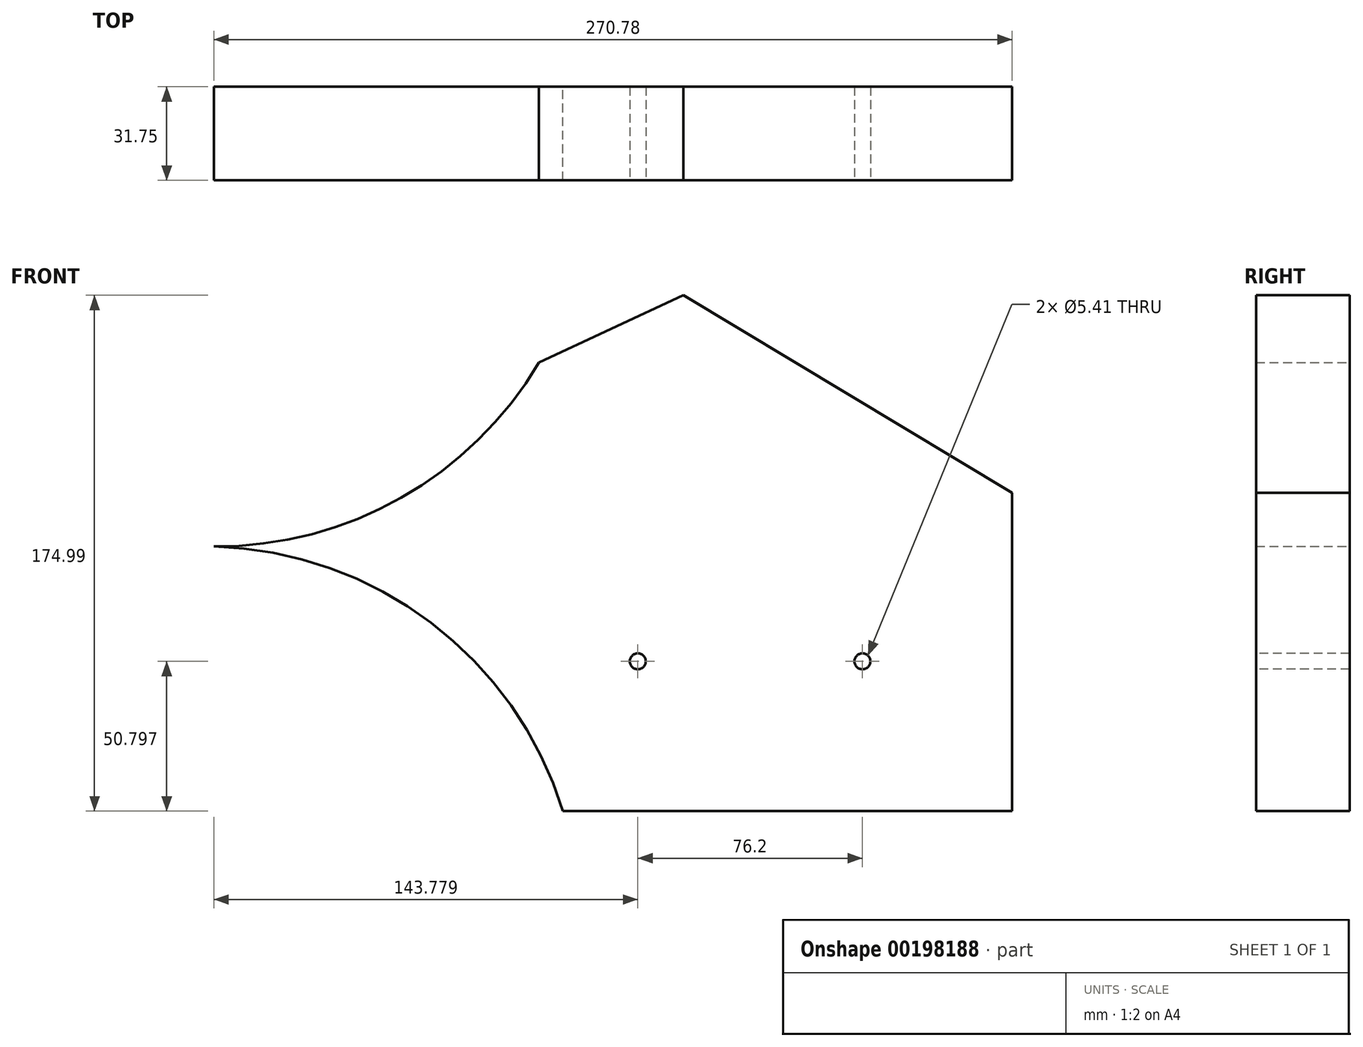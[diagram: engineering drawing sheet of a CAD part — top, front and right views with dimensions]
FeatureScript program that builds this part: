
annotation { "Feature Type Name" : "Feature", "Feature Type Description" : "" }
export const myFeature = defineFeature(function(context is Context, id is Id, definition is map)
    precondition{}
    {
        {
            var Q0;
            Q0=qCreatedBy(makeId("Front.planeOp"),FACE);
            var sketch = newSketch(context, id + "F0", { "sketchPlane" : qUnion([Q0])});
            skLineSegment(sketch, "E0", {"start": v(110.28, 62.43) * mm, "end": v(159.2, 85.24) * mm});
            skLineSegment(sketch, "E1", {"start": v(159.2, 85.24) * mm, "end": v(270.78, 18.2) * mm});
            skLineSegment(sketch, "E2", {"start": v(270.78, 18.2) * mm, "end": v(270.78, -89.75) * mm});
            skLineSegment(sketch, "E3", {"start": v(270.78, -89.75) * mm, "end": v(118.38, -89.75) * mm});
            skArc(sketch, "E4", {"start": v(0, 0) * mm, "mid": v(63.46, 16.52) * mm, "end": v(110.28, 62.43) * mm});
            skArc(sketch, "E5", {"start": v(118.38, -89.75) * mm, "mid": v(73.64, -25.82) * mm, "end": v(0, 0) * mm});
            skSolve(sketch);
        }
        {
            var Q0;
            Q0=makeQuery(id+"F0.imprint","IMPRINT",FACE,{"disambiguationData":[TD([[makeQuery(id+"F0.imprint","IMPRINT",EDGE,{"derivedFrom":sQuery(id+"F0.wireOp",EDGE,"E0")}),-1.0]])]});
            extrude(context, id + "F1", {"entities" : qUnion([Q0]), "depth" : 31.75 * mm});
        }
        {
            var Q0;
            Q0=makeQuery(id+"F1.opExtrude","CAP_FACE",FACE,{"disambiguationData":[OSD([sQuery(id+"F0.wireOp",EDGE,"E0"),sQuery(id+"F0.wireOp",EDGE,"E1"),sQuery(id+"F0.wireOp",EDGE,"E2"),sQuery(id+"F0.wireOp",EDGE,"E3"),sQuery(id+"F0.wireOp",EDGE,"E4"),sQuery(id+"F0.wireOp",EDGE,"E5")])],"isStart":false});
            var sketch = newSketch(context, id + "F2", { "sketchPlane" : qUnion([Q0])});
            skPoint(sketch, "E6", {"position": v(143.78, -38.95) * mm});
            skPoint(sketch, "E7", {"position": v(219.98, -38.95) * mm});
            skSolve(sketch);
        }
        {
            var Q0;
            Q0=sQuery(id+"F2.wireOp",VERTEX,"E6");
            var Q1;
            Q1=sQuery(id+"F2.wireOp",VERTEX,"E7");
            var Q2;
            Q2=makeQuery(id+"F1.opExtrude","SWEPT_BODY",BODY,{"disambiguationData":[OSD([sQuery(id+"F0.wireOp",EDGE,"E0"),sQuery(id+"F0.wireOp",EDGE,"E1"),sQuery(id+"F0.wireOp",EDGE,"E2"),sQuery(id+"F0.wireOp",EDGE,"E3"),sQuery(id+"F0.wireOp",EDGE,"E4"),sQuery(id+"F0.wireOp",EDGE,"E5")])]});
            hole(context, id + "F3", {"style" : HoleStyle.SIMPLE, "endStyle" : HoleEndStyle.THROUGH, "standardTappedOrClearance" : lookupTablePath({ "standard" : "ANSI", "engagement" : "75%", "pitch" : "28 tpi", "size" : "1/4", "type" : "Tapped" }), "standardBlindInLast" : lookupTablePath({ "standard" : "ANSI", "engagement" : "75%", "pitch" : "28 tpi", "size" : "1/4", "type" : "Tapped" }), "holeDiameter" : 5.4 * mm, "startFromSketch" : true, "locations" : qUnion([Q0, Q1]), "scope" : qUnion([Q2]), "isTappedThrough" : true, "majorDiameter" : 6.35 * mm, "showTappedDepth" : true});
        }
    });
